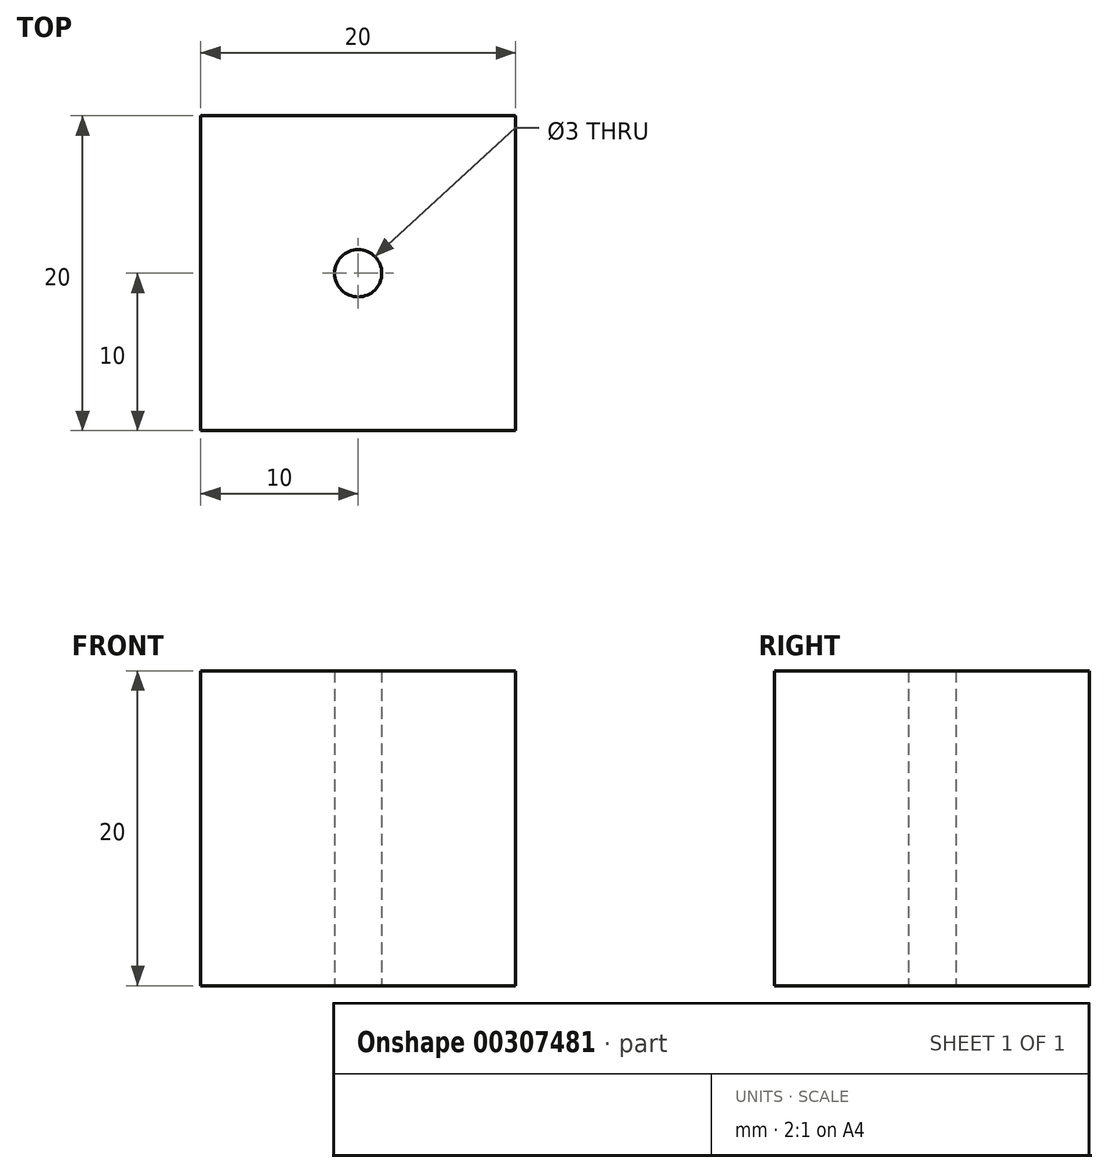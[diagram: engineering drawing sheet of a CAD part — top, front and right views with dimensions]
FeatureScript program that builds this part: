
annotation { "Feature Type Name" : "Feature", "Feature Type Description" : "" }
export const myFeature = defineFeature(function(context is Context, id is Id, definition is map)
    precondition{}
    {
        {
            var Q0;
            Q0=qCreatedBy(makeId("Top.planeOp"),FACE);
            var sketch = newSketch(context, id + "F0", { "sketchPlane" : qUnion([Q0])});
            skLineSegment(sketch, "E0.bottom", {"start": v(0, 0) * mm, "end": v(20, 0) * mm});
            skLineSegment(sketch, "E0.top", {"start": v(0, 20) * mm, "end": v(20, 20) * mm});
            skLineSegment(sketch, "E0.left", {"start": v(0, 0) * mm, "end": v(0, 20) * mm});
            skLineSegment(sketch, "E0.right", {"start": v(20, 0) * mm, "end": v(20, 20) * mm});
            skLineSegment(sketch, "E1", {"start": v(10, 20) * mm, "end": v(10, 0) * mm, "construction": true});
            skLineSegment(sketch, "E2", {"start": v(0, 10) * mm, "end": v(20, 10) * mm, "construction": true});
            skCircle(sketch, "E3", {"center": v(10, 10) * mm, "radius": 1.5 * mm});
            skSolve(sketch);
        }
        {
            var Q0;
            Q0 = qSketchRegion(id + "F0", true);
            extrude(context, id + "F1", {"entities" : qUnion([Q0]), "depth" : 20 * mm});
        }
    });
